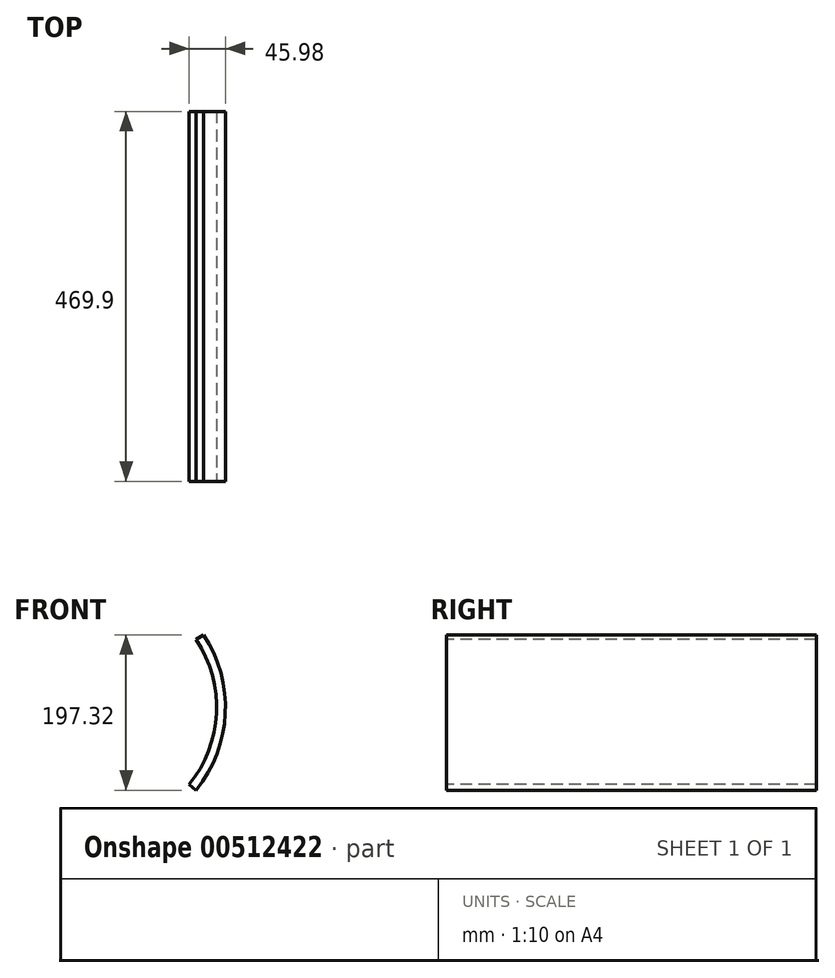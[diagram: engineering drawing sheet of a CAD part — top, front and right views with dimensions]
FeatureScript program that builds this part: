
annotation { "Feature Type Name" : "Feature", "Feature Type Description" : "" }
export const myFeature = defineFeature(function(context is Context, id is Id, definition is map)
    precondition{}
    {
        {
            var Q0;
            Q0=qCreatedBy(makeId("Front.planeOp"),FACE);
            var sketch = newSketch(context, id + "F0", { "sketchPlane" : qUnion([Q0])});
            skArc(sketch, "E0", {"start": v(11.3, -89.52) * mm, "mid": v(45.93, 1.07) * mm, "end": v(20.22, 94.59) * mm});
            skArc(sketch, "E1.0", {"start": v(19.98, -96.56) * mm, "mid": v(57.09, 0.53) * mm, "end": v(29.54, 100.76) * mm});
            skLineSegment(sketch, "E2", {"start": v(29.54, 100.76) * mm, "end": v(20.22, 94.59) * mm});
            skLineSegment(sketch, "E3", {"start": v(11.3, -89.52) * mm, "end": v(19.98, -96.56) * mm});
            skLineSegment(sketch, "E4", {"start": v(41.37, 258.13) * mm, "end": v(-33.56, 207.24) * mm});
            skSolve(sketch);
        }
        {
            var Q0;
            Q0=sQuery(id+"F0.wireOp",EDGE,"E1.0");
            var Q1;
            Q1=sQuery(id+"F0.wireOp",EDGE,"E0");
            var Q2;
            Q2=sQuery(id+"F0.wireOp",EDGE,"E2");
            var Q3;
            Q3=sQuery(id+"F0.wireOp",EDGE,"E3");
            extrude(context, id + "F1", {"bodyType" : ToolBodyType.SURFACE, "surfaceEntities" : qUnion([Q0, Q1, Q2, Q3]), "depth" : 469.9 * mm});
        }
    });
